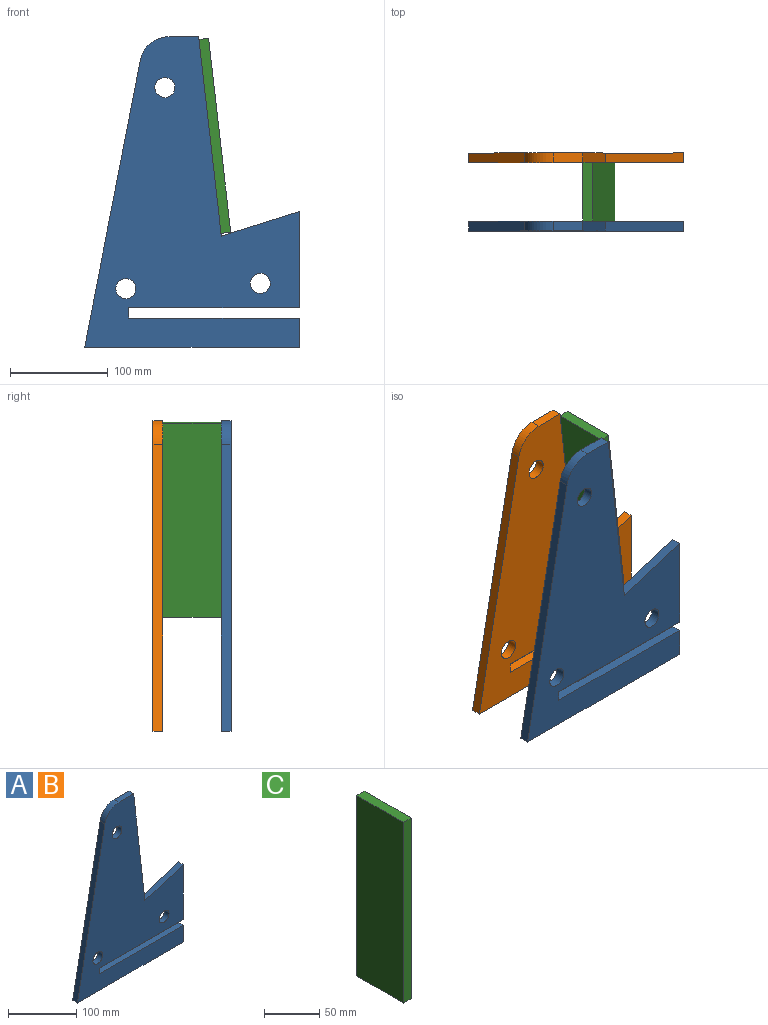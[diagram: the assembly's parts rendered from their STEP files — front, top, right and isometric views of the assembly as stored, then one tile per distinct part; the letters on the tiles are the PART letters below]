
ASSEMBLY  parts=3 mates=2
PART A: 16 faces, bbox 220x10x318.2 mm
  f0: plane 175x10mm, normal (0,0,-1), area 1750mm2, adj f1,f11,f13,f14
  f1: plane 98.68x10mm, normal (1,0,0), area 986.8mm2, adj f0,f2,f13,f14
  f2: plane 79.95x25.17mm, normal (-0.3,0,0.95), area 838.2mm2, adj f1,f3,f13,f14
  f3: plane 204.23x23.3mm, normal (0.99,0,0.11), area 2055.6mm2, adj f2,f4,f13,f14
  f4: plane 30.26x10mm, normal (0,0,1), area 302.6mm2, adj f3,f13,f14,f15
  f5: plane 293.96x57.04mm, normal (-0.98,0,0.19), area 2994.4mm2, adj f6,f13,f14,f15
  f6: plane 220x10mm, normal (0,0,-1), area 2200mm2, adj f5,f7,f13,f14
  f7: plane 30x10mm, normal (1,0,0), area 300mm2, adj f6,f8,f13,f14
  f8: plane 175x10mm, normal (0,0,1), area 1750mm2, adj f7,f11,f13,f14
  f9: cylinder r=10.25mm len=20.5mm, axis (0,1,0), area 644mm2, adj f13,f14
  f10: cylinder r=10.25mm len=20.5mm, axis (0,1,0), area 644mm2, adj f13,f14
  f11: plane 10.5x10mm, normal (1,0,0), area 105mm2, adj f0,f8,f13,f14
  f12: cylinder r=10.25mm len=20.5mm, axis (0,1,0), area 644mm2, adj f13,f14
  f13: plane 318.24x220mm, normal (0,-1,0), area 39536.9mm2, adj f0,f1,f2,f3,f4,f5,f6,f7
  f14: plane 318.24x220mm, normal (0,1,0), area 39536.9mm2, adj f0,f1,f2,f3,f4,f5,f6,f7
  f15: cylinder r=30mm len=29.45mm, axis (0,1,0), area 413.7mm2, adj f4,f5,f13,f14
PART B: same geometry as A
PART C: 6 faces, bbox 10x60x200 mm
  f0: plane 60x10mm, normal (0,0,1), area 600mm2, adj f1,f3,f4,f5
  f1: plane 200x60mm, normal (1,0,0), area 12000mm2, adj f0,f2,f4,f5
  f2: plane 60x10mm, normal (0,0,-1), area 600mm2, adj f1,f3,f4,f5
  f3: plane 200x60mm, normal (-1,0,0), area 12000mm2, adj f0,f2,f4,f5
  f4: plane 200x10mm, normal (0,1,0), area 2000mm2, adj f0,f1,f2,f3
  f5: plane 200x10mm, normal (0,-1,0), area 2000mm2, adj f0,f1,f2,f3
PLACE A t=(-32.21,-427.1,-5.01)mm
PLACE B t=(-32.21,-357.1,-5.01)mm fixed
PLACE C rot(axis=(0,1,0),173.5deg) t=(-259.67,-427.1,1895.76)mm
MATE fastened A.f3 <-> C.f1  axis (0.99,0,0.11) through (-86.01,-427.1,951.12)mm
MATE fastened B.f9 <-> A.f9  axis (0,-1,0) through (-172.21,-367.1,794.99)mm
